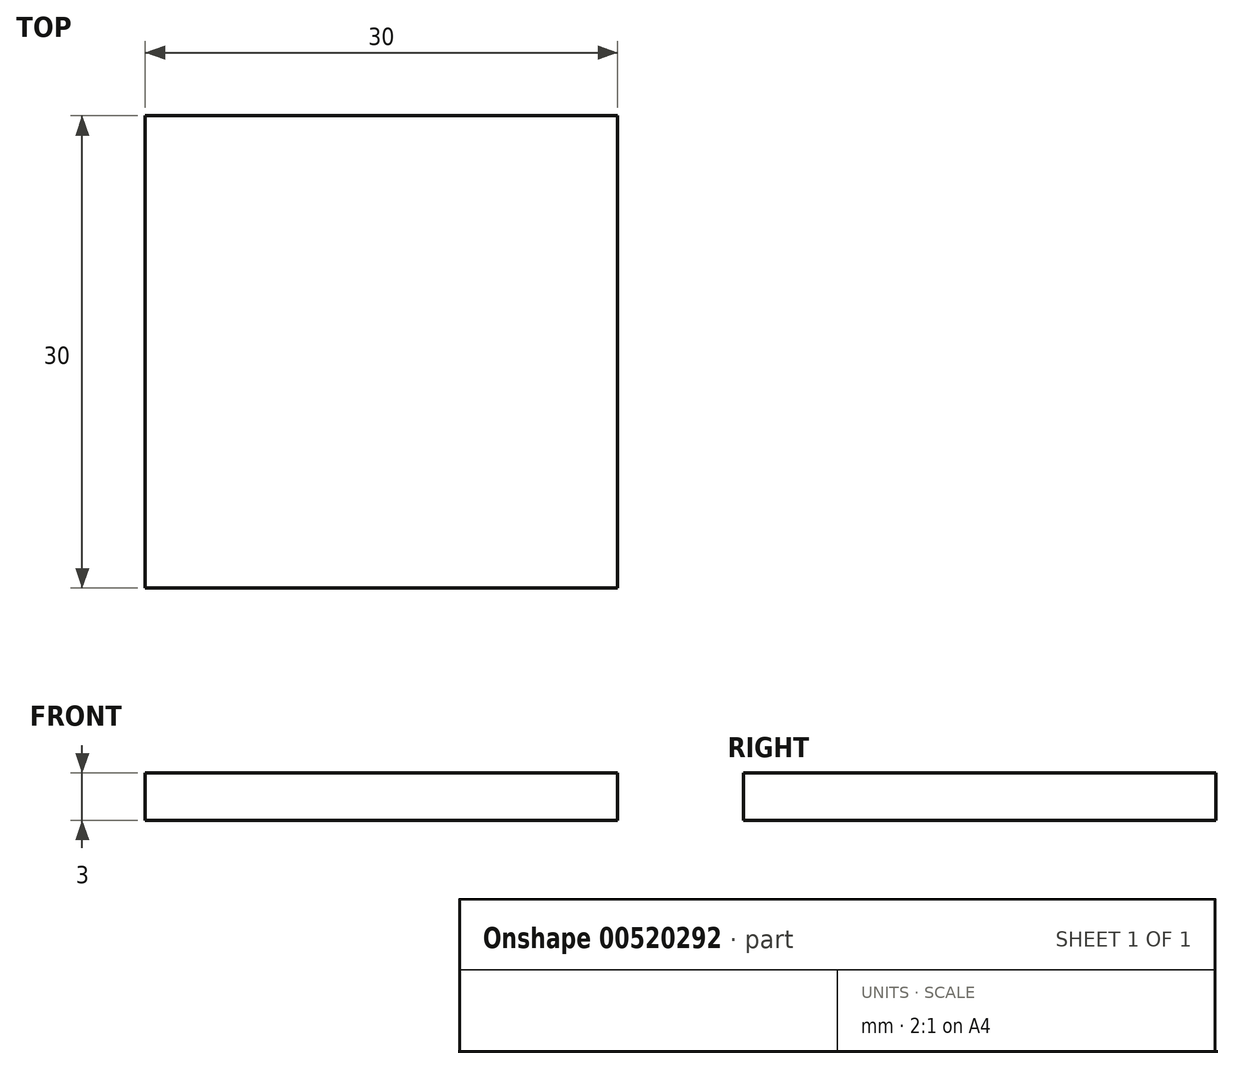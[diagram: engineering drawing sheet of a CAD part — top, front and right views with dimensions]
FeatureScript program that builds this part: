
annotation { "Feature Type Name" : "Feature", "Feature Type Description" : "" }
export const myFeature = defineFeature(function(context is Context, id is Id, definition is map)
    precondition{}
    {
        {
            var Q0;
            Q0=qCreatedBy(makeId("Top.planeOp"),FACE);
            var sketch = newSketch(context, id + "F0", { "sketchPlane" : qUnion([Q0])});
            skLineSegment(sketch, "E0.bottom", {"start": v(-15, -15) * mm, "end": v(15, -15) * mm});
            skLineSegment(sketch, "E0.top", {"start": v(-15, 15) * mm, "end": v(15, 15) * mm});
            skLineSegment(sketch, "E0.left", {"start": v(-15, -15) * mm, "end": v(-15, 15) * mm});
            skLineSegment(sketch, "E0.right", {"start": v(15, -15) * mm, "end": v(15, 15) * mm});
            skSolve(sketch);
        }
        {
            var Q0;
            Q0=makeQuery(id+"F0.imprint","IMPRINT",FACE,{"disambiguationData":[TD([[makeQuery(id+"F0.imprint","IMPRINT",EDGE,{"derivedFrom":sQuery(id+"F0.wireOp",EDGE,"E0.bottom")}),1.0]])]});
            extrude(context, id + "F1", {"entities" : qUnion([Q0]), "depth" : 3 * mm, "offsetDistance" : 25 * mm});
        }
    });
